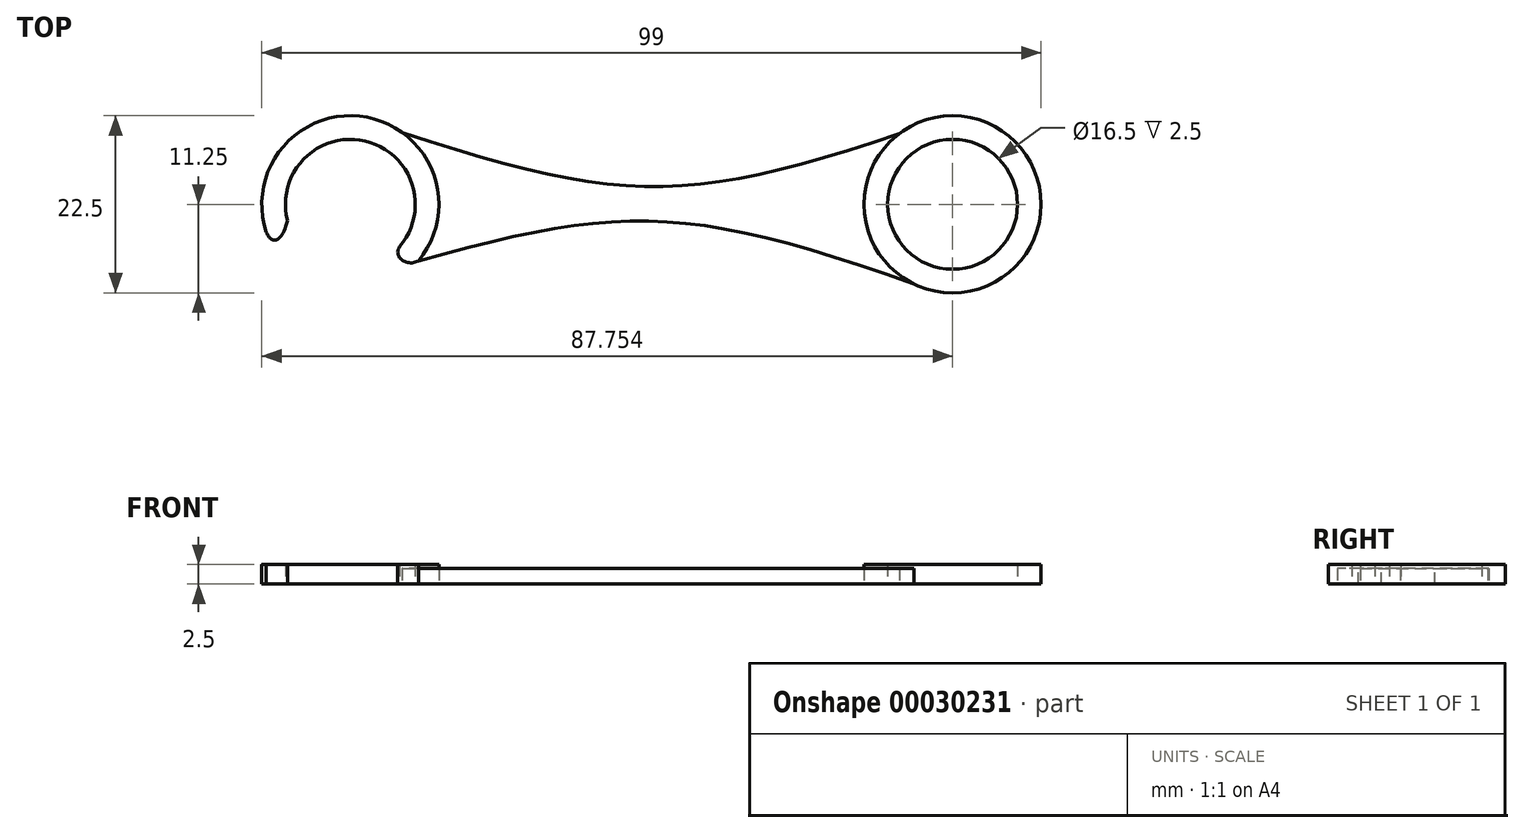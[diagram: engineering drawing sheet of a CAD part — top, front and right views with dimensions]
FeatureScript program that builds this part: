
annotation { "Feature Type Name" : "Feature", "Feature Type Description" : "" }
export const myFeature = defineFeature(function(context is Context, id is Id, definition is map)
    precondition{}
    {
        {
            var Q0;
            Q0=qCreatedBy(makeId("Top.planeOp"),FACE);
            var sketch = newSketch(context, id + "F0", { "sketchPlane" : qUnion([Q0])});
            skCircle(sketch, "E0", {"center": v(38.82, 0) * mm, "radius": 8.25 * mm});
            skCircle(sketch, "E1.1.0.0", {"center": v(-37.68, 0) * mm, "radius": 8.25 * mm});
            skLineSegment(sketch, "E1.direction1", {"start": v(38.82, 0) * mm, "end": v(-37.68, 0) * mm, "construction": true});
            skCircle(sketch, "E2", {"center": v(38.82, 0) * mm, "radius": 11.25 * mm});
            skCircle(sketch, "E3", {"center": v(-37.68, 0) * mm, "radius": 11.25 * mm});
            skFitSpline(sketch, "E4", {"points": [v(-31.08, 9.11) * mm, v(32.07, 9) * mm], "startDerivative": vector(82.92, -27.34) * mm, "endDerivative": vector(79.72, 26.99) * mm});
            skFitSpline(sketch, "E5", {"points": [v(-29.04, -7.2) * mm, v(33.94, -10.14) * mm], "startDerivative": vector(76.8, 21.61) * mm, "endDerivative": vector(85.34, -30.4) * mm});
            skFitSpline(sketch, "E6", {"points": [v(-29.04, -7.2) * mm, v(-31.13, -5.02) * mm], "startDerivative": vector(-4.9, -2.45) * mm, "endDerivative": vector(4.36, 4.41) * mm});
            skFitSpline(sketch, "E7", {"points": [v(-45.66, -2.08) * mm, v(-48.35, -3.54) * mm], "startDerivative": vector(-2.31, -8.97) * mm, "endDerivative": vector(-1.9, 4.57) * mm});
            skSolve(sketch);
        }
        {
            var Q0;
            Q0=makeQuery(id+"F0.imprint","IMPRINT",FACE,{"disambiguationData":[TD([[makeQuery(id+"F0.imprint","IMPRINT",EDGE,{"derivedFrom":sQuery(id+"F0.wireOp",EDGE,"E0")}),-1.0]])]});
            var Q1;
            {var subQ0=sQuery(id+"F0.wireOp",EDGE,"E7");Q1=makeQuery(id+"F0.imprint","IMPRINT",FACE,{"disambiguationData":[TD([[makeQuery(id+"F0.imprint","IMPRINT",EDGE,{"derivedFrom":subQ0}),-1.0]])]});}
            extrude(context, id + "F1", {"entities" : qUnion([Q0, Q1]), "depth" : 2.5 * mm});
        }
        {
            var Q0;
            {var subQ1=sQuery(id+"F0.wireOp",EDGE,"E4");Q0=makeQuery(id+"F0.imprint","IMPRINT",FACE,{"disambiguationData":[TD([[makeQuery(id+"F0.imprint","IMPRINT",EDGE,{"derivedFrom":subQ1}),-1.0]])]});}
            extrude(context, id + "F2", {"entities" : qUnion([Q0]), "depth" : 2 * mm});
        }
    });
